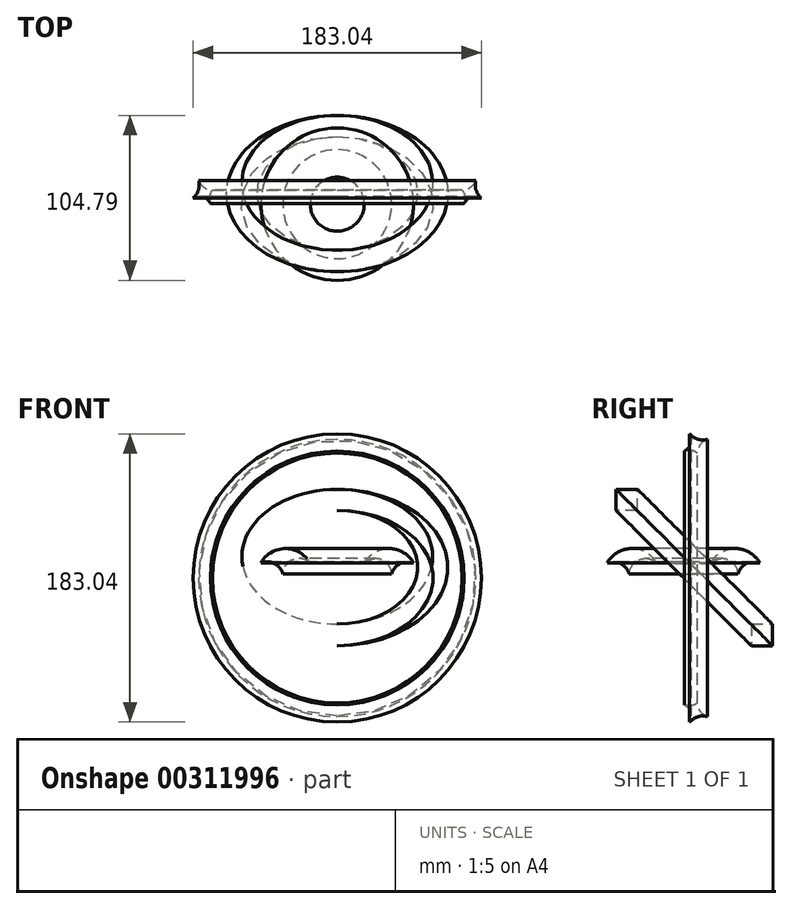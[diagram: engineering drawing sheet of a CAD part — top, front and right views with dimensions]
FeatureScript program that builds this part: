
annotation { "Feature Type Name" : "Feature", "Feature Type Description" : "" }
export const myFeature = defineFeature(function(context is Context, id is Id, definition is map)
    precondition{}
    {
        {
            var Q0;
            Q0=qCreatedBy(makeId("Right.planeOp"),FACE);
            var sketch = newSketch(context, id + "F0", { "sketchPlane" : qUnion([Q0])});
            skLineSegment(sketch, "E0", {"start": v(0, 0) * mm, "end": v(0, 26.47) * mm});
            skArc(sketch, "E1", {"start": v(34.6, 2.7) * mm, "mid": v(28, 11.64) * mm, "end": v(17.15, 9.32) * mm});
            skArc(sketch, "E2", {"start": v(48.43, 9.63) * mm, "mid": v(40, 9.2) * mm, "end": v(34.6, 2.7) * mm});
            skArc(sketch, "E3", {"start": v(48.43, 9.63) * mm, "mid": v(32.7, 18.69) * mm, "end": v(17.15, 9.32) * mm});
            skSolve(sketch);
        }
        {
            var Q0;
            Q0=makeQuery(id+"F0.imprint","IMPRINT",FACE,{"disambiguationData":[TD([[makeQuery(id+"F0.imprint","IMPRINT",EDGE,{"derivedFrom":sQuery(id+"F0.wireOp",EDGE,"E1")}),-1.0]])]});
            var Q1;
            Q1=sQuery(id+"F0.wireOp",EDGE,"E0");
            revolve(context, id + "F1", {"entities" : qUnion([Q0]), "axis" : qUnion([Q1]), "revolveType" : RevolveType.FULL});
        }
        {
            var Q0;
            Q0=qCreatedBy(makeId("Top.planeOp"),FACE);
            var sketch = newSketch(context, id + "F2", { "sketchPlane" : qUnion([Q0])});
            skLineSegment(sketch, "E4", {"start": v(0, 0) * mm, "end": v(0, 11.25) * mm});
            skArc(sketch, "E5", {"start": v(80.4, 0) * mm, "mid": v(79.66, 8.4) * mm, "end": v(72.05, 12) * mm});
            skArc(sketch, "E6", {"start": v(91.52, 3.91) * mm, "mid": v(85.07, 4.5) * mm, "end": v(80.4, 0) * mm});
            skArc(sketch, "E7", {"start": v(88, 15.04) * mm, "mid": v(88.16, 8.97) * mm, "end": v(91.52, 3.91) * mm});
            skArc(sketch, "E8", {"start": v(72.05, 12) * mm, "mid": v(80.89, 9) * mm, "end": v(88, 15.04) * mm});
            skSolve(sketch);
        }
        {
            var Q0;
            {var subQ0=sQuery(id+"F2.wireOp",EDGE,"E8");var subQ1=sQuery(id+"F2.wireOp",EDGE,"E5");var subQ2=makeQuery(id+"F2.imprint","INTERSECT",VERTEX,{"disambiguationData":[OD(0.0)],"derivedFrom":[subQ1,subQ0]});Q0=makeQuery(id+"F2.imprint","IMPRINT",FACE,{"disambiguationData":[TD([[makeQuery(id+"F2.imprint","IMPRINT",EDGE,{"disambiguationData":[TD([[subQ2,1.0]])],"derivedFrom":subQ1}),1.0]])]});}
            var Q1;
            {var subQ0=sQuery(id+"F2.wireOp",EDGE,"E6");var subQ1=sQuery(id+"F2.wireOp",EDGE,"E5");var subQ2=makeQuery(id+"F2.imprint","INTERSECT",VERTEX,{"disambiguationData":[OD(0.0)],"derivedFrom":[subQ1,subQ0]});Q1=makeQuery(id+"F2.imprint","IMPRINT",FACE,{"disambiguationData":[TD([[makeQuery(id+"F2.imprint","IMPRINT",EDGE,{"disambiguationData":[TD([[subQ2,-1.0]])],"derivedFrom":subQ1}),1.0]])]});}
            var Q2;
            {var subQ5=sQuery(id+"F2.wireOp",EDGE,"E7");Q2=makeQuery(id+"F2.imprint","IMPRINT",FACE,{"disambiguationData":[TD([[makeQuery(id+"F2.imprint","IMPRINT",EDGE,{"derivedFrom":subQ5}),-1.0]])]});}
            var Q3;
            Q3=sQuery(id+"F2.wireOp",EDGE,"E4");
            revolve(context, id + "F3", {"entities" : qUnion([Q0, Q1, Q2]), "axis" : qUnion([Q3]), "revolveType" : RevolveType.FULL});
        }
        {
            var Q0;
            Q0=qCreatedBy(makeId("Right.planeOp"),FACE);
            var sketch = newSketch(context, id + "F4", { "sketchPlane" : qUnion([Q0])});
            skLineSegment(sketch, "E9.bottom", {"start": v(-43, 56.36) * mm, "end": v(-29.26, 56.36) * mm});
            skLineSegment(sketch, "E9.top", {"start": v(-43, 43) * mm, "end": v(-29.26, 43) * mm});
            skLineSegment(sketch, "E9.left", {"start": v(-43, 56.36) * mm, "end": v(-43, 43) * mm});
            skLineSegment(sketch, "E9.right", {"start": v(-29.26, 56.36) * mm, "end": v(-29.26, 43) * mm});
            skLineSegment(sketch, "E10", {"start": v(0, 0) * mm, "end": v(40.22, 40.22) * mm});
            skSolve(sketch);
        }
        {
            var Q0;
            Q0=makeQuery(id+"F4.imprint","IMPRINT",FACE,{"disambiguationData":[TD([[makeQuery(id+"F4.imprint","IMPRINT",EDGE,{"derivedFrom":sQuery(id+"F4.wireOp",EDGE,"E9.bottom")}),-1.0]])]});
            var Q1;
            Q1=sQuery(id+"F4.wireOp",EDGE,"E10");
            revolve(context, id + "F5", {"entities" : qUnion([Q0]), "axis" : qUnion([Q1]), "revolveType" : RevolveType.FULL});
        }
    });
